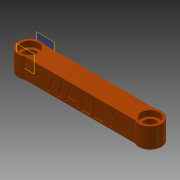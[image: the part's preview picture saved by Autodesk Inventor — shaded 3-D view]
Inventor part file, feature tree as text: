
AUTODESK INVENTOR PART (.ipt)
format: ipt  version: 2013 (Build 170138000, 138)  size: 399,360 bytes
history: native  units: mm
features: extrude x7, sketch x6, plane x2, chamfer x1, projected_geometry x1
ambient origin geometry x8: Origin, YZ Plane, XZ Plane, XY Plane, X Axis, Y Axis, Z Axis, Center Point
bodies: Solid1 (feature_tree)
feature tree (17):
  extrude  "Extrusion1"  Depth=12.5mm
  extrude  "Extrusion2"  Depth=15.1mm
  extrude  "Extrusion3"  Depth=22.1mm
  extrude  "Extrusion4"  Depth=7.0mm TaperAngle=0.0deg
  chamfer  "Chamfer1"  Distance=3.5mm Angle=45.0deg
  extrude  "Extrusion5"  Depth=10.0mm TaperAngle=0.0deg
  plane  "Work Plane2"
  sketch  "Sketch6"  dims[d27=0.5mm d28=-7.853982mm d29=0.5mm d30=-7.853982mm]
  plane  "Work Plane1"
  extrude  "Extrusion6"  Depth=0.5mm
  extrude  "Extrusion7"  [1 undecoded]
  sketch  "Sketch1"  dims[d0=150.0mm d2=12.5mm]
  sketch  "Sketch2"  dims[d3=25.0mm d4=0.0mm d5=15.1mm]
  sketch  "Sketch3"  dims[d7=0.0mm d8=0.0mm d9=22.1mm]
  sketch  "Sketch4"  dims[d11=7.0mm d12=0.0mm d13=7.0mm d14=0.0mm d15=3.5mm d16=2.0mm d17=45.0deg]
  sketch  "Sketch5"  dims[d18=3.0mm d19=10.0mm d20=0.0mm]
  projected_geometry  "Projected Loop1"
note: 1 required parameter value undecoded (feature->parameter linkage not recoverable at this tier; creation-order binding heuristic only, values carry confidence <= 0.55)
